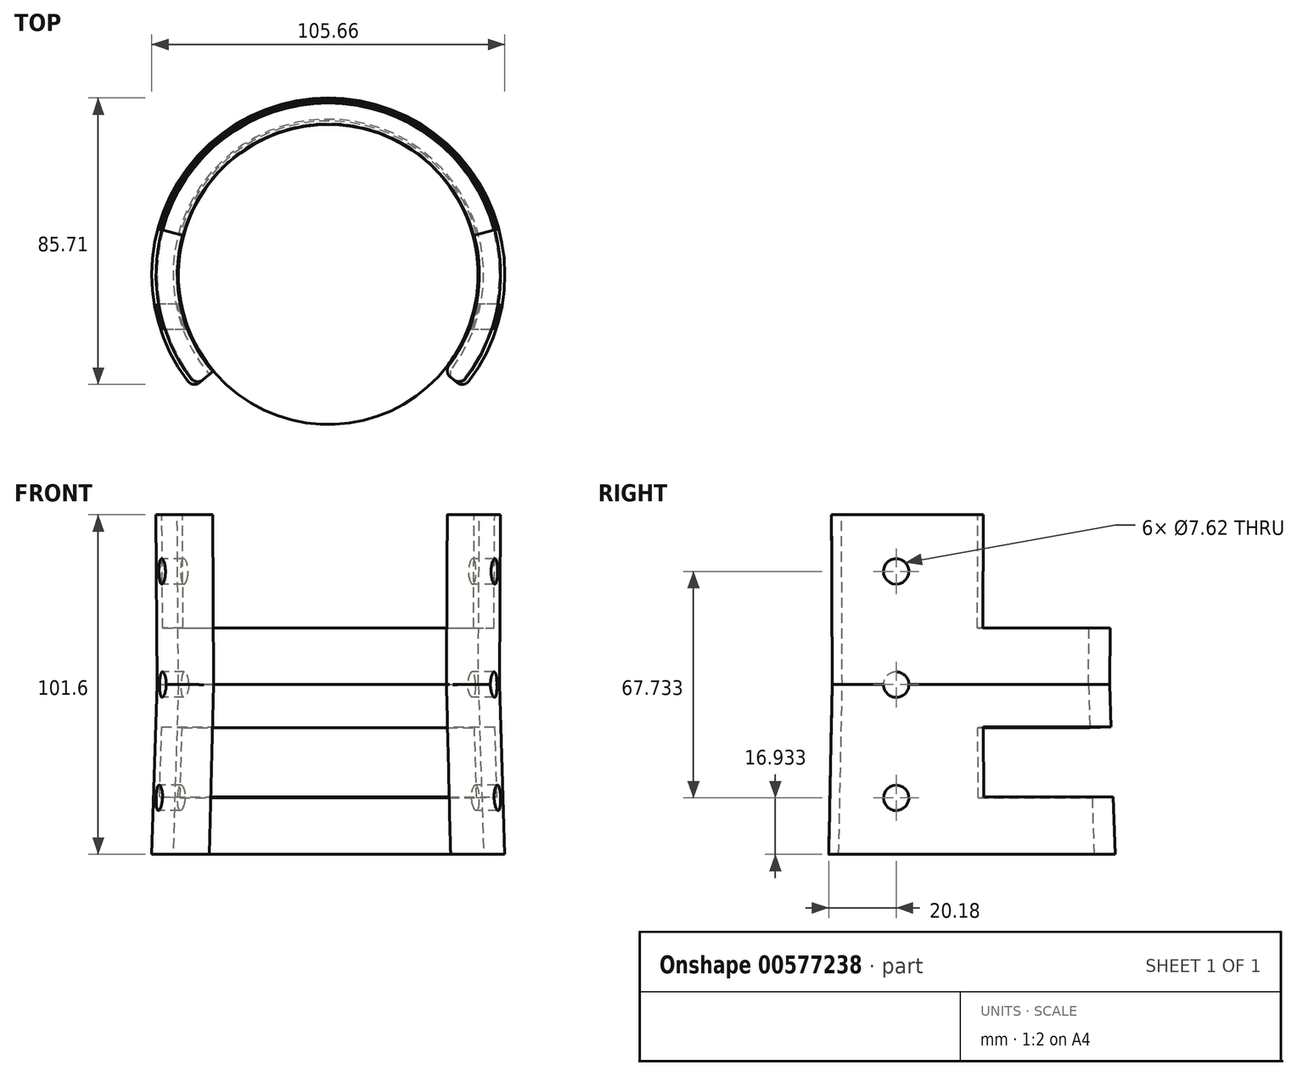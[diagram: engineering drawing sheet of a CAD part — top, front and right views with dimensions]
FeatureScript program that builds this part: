
annotation { "Feature Type Name" : "Feature", "Feature Type Description" : "" }
export const myFeature = defineFeature(function(context is Context, id is Id, definition is map)
    precondition{}
    {
        {
            var Q0;
            Q0=qCreatedBy(makeId("Front.planeOp"),FACE);
            var sketch = newSketch(context, id + "F0", { "sketchPlane" : qUnion([Q0])});
            skLineSegment(sketch, "E0", {"start": v(0, 0) * mm, "end": v(0, 50.8) * mm});
            skLineSegment(sketch, "E1", {"start": v(0, 0) * mm, "end": v(52.83, 0) * mm});
            skLineSegment(sketch, "E2", {"start": v(52.83, 0) * mm, "end": v(51.23, 50.8) * mm});
            skLineSegment(sketch, "E3", {"start": v(0, 50.8) * mm, "end": v(0, 101.6) * mm});
            skLineSegment(sketch, "E4", {"start": v(0, 101.6) * mm, "end": v(51.56, 101.6) * mm});
            skLineSegment(sketch, "E5", {"start": v(51.56, 101.6) * mm, "end": v(51.23, 50.8) * mm});
            skSolve(sketch);
        }
        {
            var Q0;
            Q0 = qSketchRegion(id + "F0", true);
            var Q1;
            Q1=sQuery(id+"F0.wireOp",EDGE,"E3");
            revolve(context, id + "F1", {"entities" : qUnion([Q0]), "axis" : qUnion([Q1]), "revolveType" : RevolveType.SYMMETRIC, "angle" : 260 * degree});
        }
        {
            var Q0;
            Q0=qCreatedBy(makeId("Front.planeOp"),FACE);
            var sketch = newSketch(context, id + "F2", { "sketchPlane" : qUnion([Q0])});
            skLineSegment(sketch, "E6", {"start": v(0, 0) * mm, "end": v(0, 50.8) * mm});
            skLineSegment(sketch, "E7", {"start": v(0, 50.8) * mm, "end": v(0, 101.6) * mm});
            skLineSegment(sketch, "E8", {"start": v(0, 101.6) * mm, "end": v(45.21, 101.6) * mm});
            skLineSegment(sketch, "E9", {"start": v(0, 0) * mm, "end": v(46.48, 0) * mm});
            skLineSegment(sketch, "E10", {"start": v(0, 50.8) * mm, "end": v(44.88, 50.8) * mm, "construction": true});
            skLineSegment(sketch, "E11", {"start": v(44.88, 50.8) * mm, "end": v(45.21, 101.6) * mm});
            skLineSegment(sketch, "E12", {"start": v(44.88, 50.8) * mm, "end": v(46.48, 0) * mm});
            skSolve(sketch);
        }
        {
            var Q0;
            Q0 = qSketchRegion(id + "F2", true);
            var Q1;
            Q1=sQuery(id+"F2.wireOp",EDGE,"E7");
            revolve(context, id + "F3", {"operationType" : NewBodyOperationType.REMOVE, "entities" : qUnion([Q0]), "axis" : qUnion([Q1]), "revolveType" : RevolveType.FULL, "oppositeDirection" : true});
        }
        {
            var Q0;
            Q0=makeQuery(id+"F3.boolean.opBoolean","INTERSECT",EDGE,{"disambiguationData":[OD(1.0)],"derivedFrom":[makeQuery(id+"F1.opRevolve","CAP_FACE",FACE,{"disambiguationData":[OSD([sQuery(id+"F0.wireOp",EDGE,"E0"),sQuery(id+"F0.wireOp",EDGE,"E1"),sQuery(id+"F0.wireOp",EDGE,"E2"),sQuery(id+"F0.wireOp",EDGE,"E3"),sQuery(id+"F0.wireOp",EDGE,"E4"),sQuery(id+"F0.wireOp",EDGE,"E5")])],"isStart":true}),makeQuery(id+"F3.opRevolve","SWEPT_FACE",FACE,{"disambiguationData":[OSD([sQuery(id+"F2.wireOp",EDGE,"E11")])]})]});
            var Q1;
            Q1=makeQuery(id+"F3.boolean.opBoolean","INTERSECT",EDGE,{"disambiguationData":[OD(0.0)],"derivedFrom":[makeQuery(id+"F1.opRevolve","CAP_FACE",FACE,{"disambiguationData":[OSD([sQuery(id+"F0.wireOp",EDGE,"E0"),sQuery(id+"F0.wireOp",EDGE,"E1"),sQuery(id+"F0.wireOp",EDGE,"E2"),sQuery(id+"F0.wireOp",EDGE,"E3"),sQuery(id+"F0.wireOp",EDGE,"E4"),sQuery(id+"F0.wireOp",EDGE,"E5")])],"isStart":true}),makeQuery(id+"F3.opRevolve","SWEPT_FACE",FACE,{"disambiguationData":[OSD([sQuery(id+"F2.wireOp",EDGE,"E11")])]})]});
            var Q2;
            Q2=makeQuery(id+"F1.opRevolve","CAP_EDGE",EDGE,{"disambiguationData":[OSD([sQuery(id+"F0.wireOp",EDGE,"E5")])],"isStart":true});
            var Q3;
            Q3=makeQuery(id+"F1.opRevolve","CAP_EDGE",EDGE,{"disambiguationData":[OSD([sQuery(id+"F0.wireOp",EDGE,"E5")])],"isStart":false});
            var Q4;
            Q4=makeQuery(id+"F3.boolean.opBoolean","INTERSECT",EDGE,{"disambiguationData":[OD(1.0)],"derivedFrom":[makeQuery(id+"F1.opRevolve","CAP_FACE",FACE,{"disambiguationData":[OSD([sQuery(id+"F0.wireOp",EDGE,"E0"),sQuery(id+"F0.wireOp",EDGE,"E1"),sQuery(id+"F0.wireOp",EDGE,"E2"),sQuery(id+"F0.wireOp",EDGE,"E3"),sQuery(id+"F0.wireOp",EDGE,"E4"),sQuery(id+"F0.wireOp",EDGE,"E5")])],"isStart":true}),makeQuery(id+"F3.opRevolve","SWEPT_FACE",FACE,{"disambiguationData":[OSD([sQuery(id+"F2.wireOp",EDGE,"E12")])]})]});
            var Q5;
            Q5=makeQuery(id+"F1.opRevolve","CAP_EDGE",EDGE,{"disambiguationData":[OSD([sQuery(id+"F0.wireOp",EDGE,"E2")])],"isStart":false});
            var Q6;
            Q6=makeQuery(id+"F3.boolean.opBoolean","INTERSECT",EDGE,{"disambiguationData":[OD(0.0)],"derivedFrom":[makeQuery(id+"F1.opRevolve","CAP_FACE",FACE,{"disambiguationData":[OSD([sQuery(id+"F0.wireOp",EDGE,"E0"),sQuery(id+"F0.wireOp",EDGE,"E1"),sQuery(id+"F0.wireOp",EDGE,"E2"),sQuery(id+"F0.wireOp",EDGE,"E3"),sQuery(id+"F0.wireOp",EDGE,"E4"),sQuery(id+"F0.wireOp",EDGE,"E5")])],"isStart":true}),makeQuery(id+"F3.opRevolve","SWEPT_FACE",FACE,{"disambiguationData":[OSD([sQuery(id+"F2.wireOp",EDGE,"E12")])]})]});
            var Q7;
            Q7=makeQuery(id+"F1.opRevolve","CAP_EDGE",EDGE,{"disambiguationData":[OSD([sQuery(id+"F0.wireOp",EDGE,"E2")])],"isStart":true});
            fillet(context, id + "F4", {"entities" : qUnion([Q0, Q1, Q2, Q3, Q4, Q5, Q6, Q7]), "radius" : 2.54 * mm, "tangentPropagation" : true, "allowEdgeOverflow" : false});
        }
        {
            var Q0;
            Q0=qCreatedBy(makeId("Front.planeOp"),FACE);
            var sketch = newSketch(context, id + "F5", { "sketchPlane" : qUnion([Q0])});
            skLineSegment(sketch, "E13", {"start": v(0, 0) * mm, "end": v(0, 50.8) * mm, "construction": true});
            skLineSegment(sketch, "E14", {"start": v(0, 50.8) * mm, "end": v(0, 101.6) * mm, "construction": true});
            skLineSegment(sketch, "E15", {"start": v(0, 101.6) * mm, "end": v(51.56, 101.6) * mm, "construction": true});
            skLineSegment(sketch, "E16", {"start": v(0, 0) * mm, "end": v(52.83, 0) * mm, "construction": true});
            skLineSegment(sketch, "E17", {"start": v(51.56, 101.6) * mm, "end": v(51.23, 50.8) * mm, "construction": true});
            skLineSegment(sketch, "E18", {"start": v(51.23, 50.8) * mm, "end": v(52.83, 0) * mm, "construction": true});
            skLineSegment(sketch, "E19", {"start": v(52.83, 0) * mm, "end": v(46.48, 0) * mm});
            skLineSegment(sketch, "E20", {"start": v(51.23, 50.8) * mm, "end": v(44.88, 50.8) * mm, "construction": true});
            skLineSegment(sketch, "E21", {"start": v(51.56, 101.6) * mm, "end": v(45.21, 101.6) * mm, "construction": true});
            skLineSegment(sketch, "E22", {"start": v(45.21, 101.6) * mm, "end": v(44.88, 50.8) * mm, "construction": true});
            skLineSegment(sketch, "E23", {"start": v(44.88, 50.8) * mm, "end": v(46.48, 0) * mm, "construction": true});
            skLineSegment(sketch, "E24", {"start": v(0, 0) * mm, "end": v(0, 16.93) * mm, "construction": true});
            skLineSegment(sketch, "E25", {"start": v(0, 16.93) * mm, "end": v(0, 33.87) * mm, "construction": true});
            skLineSegment(sketch, "E26", {"start": v(0, 50.8) * mm, "end": v(0, 67.73) * mm, "construction": true});
            skLineSegment(sketch, "E27", {"start": v(0, 67.73) * mm, "end": v(0, 84.67) * mm, "construction": true});
            skLineSegment(sketch, "E28", {"start": v(45.42, 33.66) * mm, "end": v(45.95, 16.93) * mm});
            skLineSegment(sketch, "E29", {"start": v(52.3, 17.13) * mm, "end": v(51.73, 35) * mm});
            skLineSegment(sketch, "E30", {"start": v(45, 67.73) * mm, "end": v(45.1, 84.37) * mm});
            skLineSegment(sketch, "E31", {"start": v(45, 67.73) * mm, "end": v(51.34, 67.7) * mm});
            skLineSegment(sketch, "E32", {"start": v(51.34, 67.7) * mm, "end": v(51.45, 84.37) * mm});
            skLineSegment(sketch, "E33", {"start": v(45.21, 101.6) * mm, "end": v(51.56, 101.6) * mm});
            skLineSegment(sketch, "E34", {"start": v(51.45, 84.37) * mm, "end": v(51.56, 101.6) * mm});
            skLineSegment(sketch, "E35", {"start": v(45.21, 101.6) * mm, "end": v(45.1, 84.37) * mm});
            skLineSegment(sketch, "E36", {"start": v(45.42, 33.66) * mm, "end": v(45.29, 37.89) * mm});
            skLineSegment(sketch, "E37", {"start": v(51.73, 35) * mm, "end": v(51.63, 38.17) * mm});
            skLineSegment(sketch, "E38", {"start": v(51.63, 38.17) * mm, "end": v(45.29, 37.89) * mm});
            skLineSegment(sketch, "E39", {"start": v(45.95, 16.93) * mm, "end": v(52.3, 17.13) * mm});
            skSolve(sketch);
        }
        {
            var Q0;
            Q0 = qSketchRegion(id + "F5", true);
            var Q1;
            Q1=sQuery(id+"F2.wireOp",EDGE,"E7");
            revolve(context, id + "F6", {"operationType" : NewBodyOperationType.REMOVE, "entities" : qUnion([Q0]), "axis" : qUnion([Q1]), "revolveType" : RevolveType.SYMMETRIC, "angle" : 150 * degree});
        }
        {
            var Q0;
            Q0=qCreatedBy(makeId("Front.planeOp"),FACE);
            var sketch = newSketch(context, id + "F7", { "sketchPlane" : qUnion([Q0])});
            skLineSegment(sketch, "E40", {"start": v(0, 0) * mm, "end": v(0, 16.93) * mm, "construction": true});
            skLineSegment(sketch, "E41", {"start": v(0, 16.93) * mm, "end": v(0, 33.87) * mm, "construction": true});
            skLineSegment(sketch, "E42", {"start": v(0, 33.87) * mm, "end": v(0, 50.8) * mm, "construction": true});
            skLineSegment(sketch, "E43", {"start": v(0, 50.8) * mm, "end": v(0, 67.73) * mm, "construction": true});
            skLineSegment(sketch, "E44", {"start": v(0, 67.73) * mm, "end": v(0, 84.67) * mm, "construction": true});
            skLineSegment(sketch, "E45", {"start": v(0, 16.93) * mm, "end": v(-12.7, 16.93) * mm, "construction": true});
            skLineSegment(sketch, "E46", {"start": v(0, 50.8) * mm, "end": v(-12.7, 50.8) * mm, "construction": true});
            skLineSegment(sketch, "E47", {"start": v(0, 84.67) * mm, "end": v(-12.7, 84.67) * mm, "construction": true});
            skCircle(sketch, "E48", {"center": v(-12.7, 84.67) * mm, "radius": 3.81 * mm});
            skCircle(sketch, "E49", {"center": v(-12.7, 50.8) * mm, "radius": 3.81 * mm});
            skCircle(sketch, "E50", {"center": v(-12.7, 16.93) * mm, "radius": 3.81 * mm});
            skSolve(sketch);
        }
        {
            var Q0;
            Q0 = qSketchRegion(id + "F7", true);
            extrude(context, id + "F8", {"entities" : qUnion([Q0]), "operationType" : NewBodyOperationType.REMOVE, "endBound" : BoundingType.SYMMETRIC, "depth" : 127 * mm, "offsetDistance" : 25.4 * mm});
        }
        {
            var Q0;
            Q0=makeQuery(id+"F1.opRevolve","SWEPT_BODY",BODY,{"disambiguationData":[OSD([sQuery(id+"F0.wireOp",EDGE,"E0"),sQuery(id+"F0.wireOp",EDGE,"E1"),sQuery(id+"F0.wireOp",EDGE,"E2"),sQuery(id+"F0.wireOp",EDGE,"E3"),sQuery(id+"F0.wireOp",EDGE,"E4"),sQuery(id+"F0.wireOp",EDGE,"E5")])]});
            var Q1;
            Q1=sQuery(id+"F2.wireOp",EDGE,"E7");
            transform(context, id + "F9", {"entities" : qUnion([Q0]), "transformType" : TransformType.ROTATION, "transformAxis" : qUnion([Q1]), "angle" : 90 * degree, "makeCopy" : false});
        }
    });
